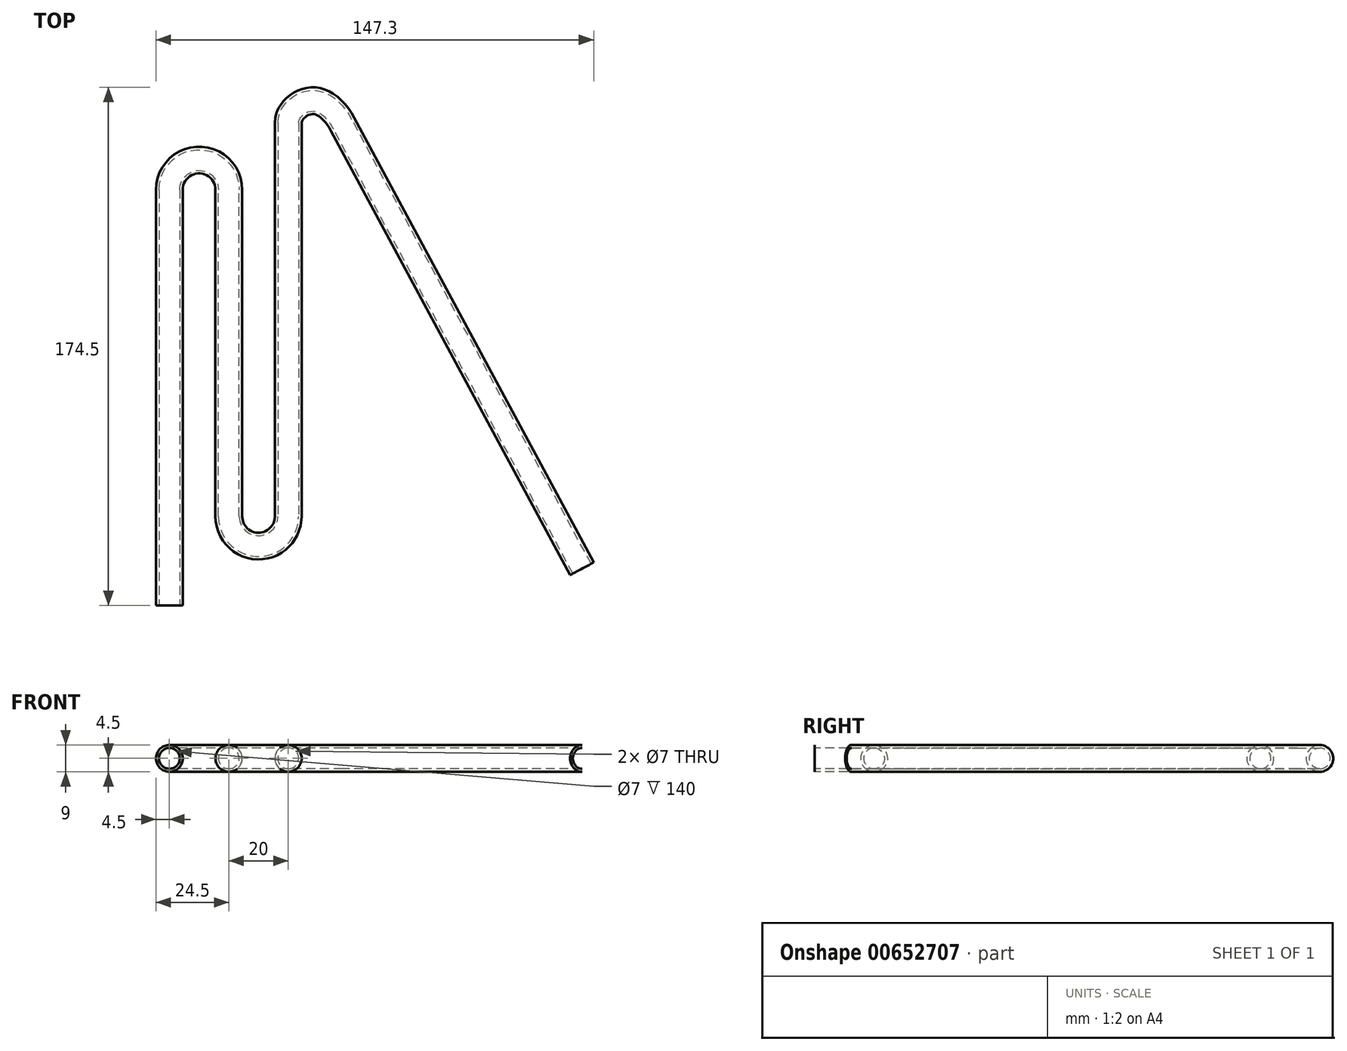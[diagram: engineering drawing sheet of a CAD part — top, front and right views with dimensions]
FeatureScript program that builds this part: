
annotation { "Feature Type Name" : "Feature", "Feature Type Description" : "" }
export const myFeature = defineFeature(function(context is Context, id is Id, definition is map)
    precondition{}
    {
        {
            var Q0;
            Q0=qCreatedBy(makeId("Top.planeOp"),FACE);
            var sketch = newSketch(context, id + "F0", { "sketchPlane" : qUnion([Q0])});
            skLineSegment(sketch, "E0", {"start": v(-40, -99.53) * mm, "end": v(-40, 40.47) * mm});
            skArc(sketch, "E1", {"start": v(-20, 40.47) * mm, "mid": v(-30, 50.47) * mm, "end": v(-40, 40.47) * mm});
            skLineSegment(sketch, "E2", {"start": v(-20, 40.47) * mm, "end": v(-20, -69.53) * mm});
            skArc(sketch, "E3", {"start": v(-20, -69.53) * mm, "mid": v(-10, -79.53) * mm, "end": v(0, -69.53) * mm});
            skLineSegment(sketch, "E4", {"start": v(0, -69.53) * mm, "end": v(0, 62.97) * mm});
            skLineSegment(sketch, "E5", {"start": v(18.26, 62.55) * mm, "end": v(98.84, -87.14) * mm});
            skFitSpline(sketch, "E6", {"points": [v(0, 62.97) * mm, v(8.1, 70.47) * mm, v(18.26, 62.55) * mm], "startDerivative": vector(0, 25.2) * mm, "endDerivative": vector(13.1, -24.55) * mm});
            skLineSegment(sketch, "E7", {"start": v(-30, 50.47) * mm, "end": v(-50.03, 50.47) * mm, "construction": true});
            skLineSegment(sketch, "E8", {"start": v(-10, -79.53) * mm, "end": v(16.8, -79.53) * mm, "construction": true});
            skLineSegment(sketch, "E9", {"start": v(8.1, 70.47) * mm, "end": v(-14.96, 70.47) * mm, "construction": true});
            skLineSegment(sketch, "E10", {"start": v(-40, -99.53) * mm, "end": v(19.35, -99.53) * mm, "construction": true});
            skSolve(sketch);
        }
        {
            var Q0;
            Q0=qCreatedBy(makeId("Front.planeOp"),FACE);
            var sketch = newSketch(context, id + "F1", { "sketchPlane" : qUnion([Q0])});
            skPoint(sketch, "E11.0", {"position": v(-40, 0) * mm});
            skCircle(sketch, "E12", {"center": v(-40, 0) * mm, "radius": 4.5 * mm});
            skCircle(sketch, "E13", {"center": v(-40, 0) * mm, "radius": 3.5 * mm});
            skSolve(sketch);
        }
        {
            var Q0;
            Q0=makeQuery(id+"F1.imprint","IMPRINT",FACE,{"disambiguationData":[TD([[makeQuery(id+"F1.imprint","IMPRINT",EDGE,{"derivedFrom":sQuery(id+"F1.wireOp",EDGE,"E12")}),1.0]])]});
            var Q1;
            Q1=sQuery(id+"F0.wireOp",EDGE,"E0");
            var Q2;
            Q2=sQuery(id+"F0.wireOp",EDGE,"E1");
            var Q3;
            Q3=sQuery(id+"F0.wireOp",EDGE,"E2");
            var Q4;
            Q4=sQuery(id+"F0.wireOp",EDGE,"E3");
            var Q5;
            Q5=sQuery(id+"F0.wireOp",EDGE,"E4");
            var Q6;
            Q6=sQuery(id+"F0.wireOp",EDGE,"E6");
            var Q7;
            Q7=sQuery(id+"F0.wireOp",EDGE,"E5");
            sweep(context, id + "F2", {"profiles" : qUnion([Q0]), "path" : qUnion([Q1, Q2, Q3, Q4, Q5, Q6, Q7])});
        }
    });
